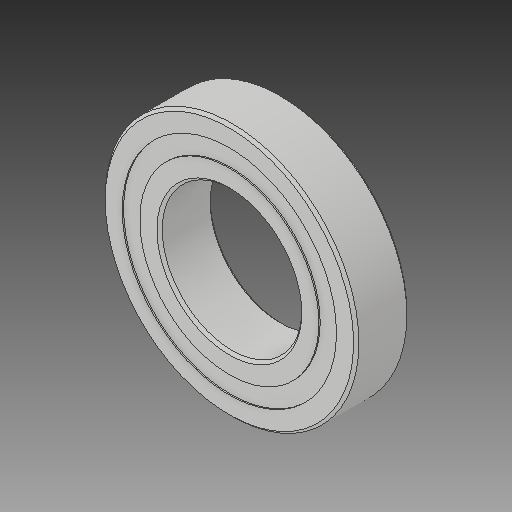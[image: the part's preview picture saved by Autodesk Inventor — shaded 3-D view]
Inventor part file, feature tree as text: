
AUTODESK INVENTOR PART (.ipt)
format: ipt  version: 2019 (Build 230136000, 136)  size: 592,896 bytes
history: native  units: in
note: dims shown in document units (in); Inventor stores cm internally (conversion verified against a paired STEP export)
features: other x11, revolve x5
ambient origin geometry x8: Origin, YZ Plane, XZ Plane, XY Plane, X Axis, Y Axis, Z Axis, Center Point
bodies: Solid1 (feature_tree), Solid2 (feature_tree), Solid3 (feature_tree), Solid4 (feature_tree), Solid5 (feature_tree), Solid6 (feature_tree), Solid7 (feature_tree), Solid8 (feature_tree), Solid9 (feature_tree), Solid10 (feature_tree), Solid11 (feature_tree), Solid12 (feature_tree), Solid13 (feature_tree), Solid14 (feature_tree), Solid15 (feature_tree), Solid16 (feature_tree)
feature tree (16):
  revolve  "Revolve1"  [1 undecoded]
  revolve  "Revolve3"  [1 undecoded]
  revolve  "Revolve4"  [1 undecoded]
  other  "CirPattern1[1]"
  other  "CirPattern1[2]"
  other  "CirPattern1[3]"
  other  "CirPattern1[4]"
  other  "CirPattern1[5]"
  other  "CirPattern1[6]"
  other  "CirPattern1[7]"
  other  "CirPattern1[8]"
  other  "CirPattern1[9]"
  other  "CirPattern1[10]"
  other  "CirPattern1[11]"
  revolve  "Revolve5[1]"  [1 undecoded]
  revolve  "Revolve5[2]"  [1 undecoded]
note: 5 required parameter values undecoded (feature->parameter linkage not recoverable at this tier; creation-order binding heuristic only, values carry confidence <= 0.55)
